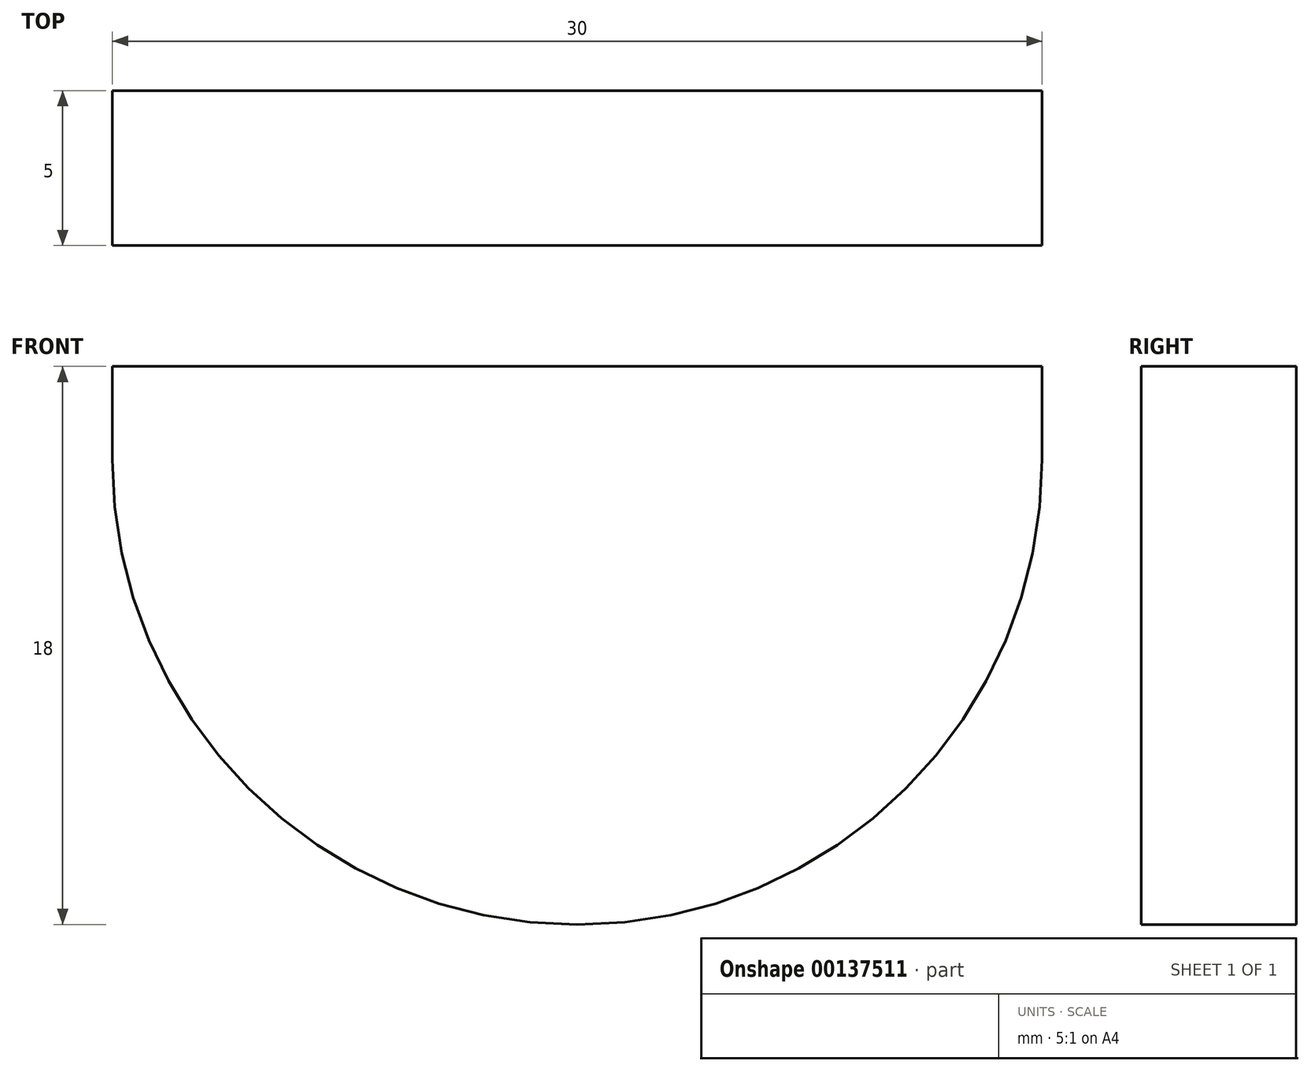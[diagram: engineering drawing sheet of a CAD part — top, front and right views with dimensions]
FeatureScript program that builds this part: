
annotation { "Feature Type Name" : "Feature", "Feature Type Description" : "" }
export const myFeature = defineFeature(function(context is Context, id is Id, definition is map)
    precondition{}
    {
        {
            var Q0;
            Q0=qCreatedBy(makeId("Front.planeOp"),FACE);
            var sketch = newSketch(context, id + "F0", { "sketchPlane" : qUnion([Q0])});
            skLineSegment(sketch, "E0", {"start": v(0, 0) * mm, "end": v(15, 0) * mm});
            skLineSegment(sketch, "E1", {"start": v(15, 0) * mm, "end": v(-15, 0) * mm});
            skLineSegment(sketch, "E2", {"start": v(-15, 0) * mm, "end": v(-15, 3) * mm});
            skLineSegment(sketch, "E3", {"start": v(-15, 3) * mm, "end": v(15, 3) * mm});
            skLineSegment(sketch, "E4", {"start": v(15, 3) * mm, "end": v(15, 0) * mm});
            skArc(sketch, "E5", {"start": v(-15, 0) * mm, "mid": v(0, -15) * mm, "end": v(15, 0) * mm});
            skSolve(sketch);
        }
        {
            var Q0;
            Q0 = qSketchRegion(id + "F0", true);
            extrude(context, id + "F1", {"entities" : qUnion([Q0]), "depth" : 5 * mm, "symmetric" : true});
        }
    });
